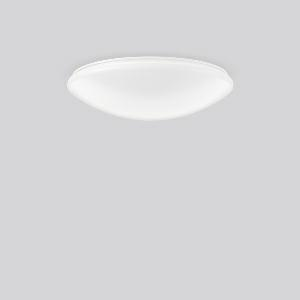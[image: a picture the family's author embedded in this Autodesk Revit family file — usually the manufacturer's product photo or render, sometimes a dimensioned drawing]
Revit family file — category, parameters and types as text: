
# Revit family: flat_polymero_311592_002_76_afa9
name_source: partatom
category: Lighting Fixtures
units: mm (PartAtom-declared; Revit-internal decimal feet)

## family parameters
Cut with Voids When Loaded = No
Host = Face
Light Source = No
Part Type = Normal
Room Calculation Point = No
Round Connector Dimension = Use Diameter
Shared = No

## types (1)
- FLAT POLYMERO (1 x LED Modul 830, 1800 lm, 3000)
    Apparent Load = 18 VA
    CIE Flux Codes = 43 72 90 90 100
    Color Rendering = 80
    Color Temperature = 3000
    Default Elevation = 1800 mm  [stored 5.90551 ft]
    Description = Series: FLAT POLYMERO
Decorative round surface-mounted luminaire. Base: metal, powder-coated. Diffuser made of non-yellowing plastic (PMMA), opal. Diffuser fastening: patented push system. Suitable for Ceiling mounting, Wall (surface). 
Colour: white
Diameter: 460 mm
Height: 120 mm
Lamp: LED
Socket: without socket
Colour temperature: 3000K
Colour rendering index (CRI): 80
System power: 18 W
Rated luminous flux: 1800 lm
Beam angle Down: 116°
Luminous efficiency: 100 lm/W
Control gear: Converter, dimmable, DALI
Protection class: I
Type of protection: IP 40
    Height = 120 mm
    Lamp = 1 x LED Modul 830
    Lamp Light Flux = 1800 lm
    Lamp count = 1
    Length = 460 mm
    Lifetime = 50000 h
    Luminous efficacy = 100 lm/W
    Manufacturer = RZB
    ModVariant = No
    Model = 311592.002.76
    Mounting Place = Ceiling, Wall
    Mounting Type = Surface mounted
    Number of Poles = 1
    OnlyDefault = Yes
    Power Factor = 1
    Product Name = FLAT POLYMERO
    Product group = Surface mounted ceiling and wall luminaires
    ProductGroupID = 305
    Protection Class = Protection class I
    Protection Degree = IP 40
    RLX_Detail_Level = 1
    RLX_Emergency_Light_Flux = 0 lm
    RLX_Emergency_Type = 0
    RLX_Emergency_Type_DB = No
    RlxData = <blob elided: 74249 chars, md5=10959ee5>
    Socket = socket
    Standby Power = 0 W
    System Light Flux = 1800 lm
    System Power = 18 W
    Type Comments = ALEA SPOT
    Type Image = 311518.002.1.jpg
    URL = http://relux.com
    VarID = ---
    Voltage = 230 V
    Voltage Range = 220-240 V
    Weight = 0.00 kg
    Width = 0 mm  [stored 0 ft]

note: [stored X ft] marks values corroborated as IEEE doubles in the binary element streams (Revit-internal decimal feet)

## geometry (parser evidence)
native form markers: Blend x4, Sweep x10
no freeform markers — native parametric forms only
